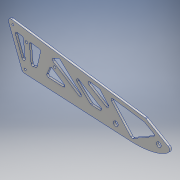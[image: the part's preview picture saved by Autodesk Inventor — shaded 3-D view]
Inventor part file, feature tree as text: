
AUTODESK INVENTOR PART (.ipt)
format: ipt  version: 2018 (Build 220112000, 112)  size: 1,370,624 bytes
history: native  units: mm
features: extrude x4, sketch x4, projected_geometry x3, fillet x1
ambient origin geometry x8: Origin, YZ Plane, XZ Plane, XY Plane, X Axis, Y Axis, Z Axis, Center Point
bodies: Body1 (feature_tree)
feature tree (12):
  extrude  "押し出し3"  TaperAngle=30.0deg  [1 undecoded]
  fillet  "フィレット2"  Radius=5.0mm
  sketch  "スケッチ4"
  extrude  "押し出し7"  Depth=6.0mm
  extrude  "押し出し9"  Depth=5.0mm
  extrude  "押し出し13"  Depth=10.0mm
  sketch  "スケッチ2"
  projected_geometry  "投影ループ4"
  projected_geometry  "投影ループ5"
  sketch  "スケッチ6"
  sketch  "スケッチ10"
  projected_geometry  "投影ループ6"
note: 1 required parameter value undecoded (feature->parameter linkage not recoverable at this tier; creation-order binding heuristic only, values carry confidence <= 0.55)
